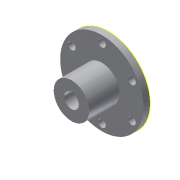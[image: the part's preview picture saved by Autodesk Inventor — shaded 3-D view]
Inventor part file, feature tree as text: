
AUTODESK INVENTOR PART (.ipt)
format: ipt  version: 2013 (Build 170138000, 138)  size: 117,760 bytes
history: native  units: in
note: dims shown in document units (in); Inventor stores cm internally (conversion verified against a paired STEP export)
features: extrude x4, sketch x4, pattern_circular x1
ambient origin geometry x8: Origin, YZ Plane, XZ Plane, XY Plane, X Axis, Y Axis, Z Axis, Center Point
bodies: Solid1 (feature_tree)
feature tree (9):
  extrude  "Extrusion1"  Depth=0.18in TaperAngle=0.0deg
  extrude  "Extrusion2"  Depth=0.82in TaperAngle=0.0deg
  extrude  "Extrusion3"  Depth=0.0984in
  extrude  "Extrusion4"  Depth=0.82in TaperAngle=0.0deg
  pattern_circular  "Circular Pattern1"  [2 undecoded]
  sketch  "Sketch1"  dims[d0=2.25in d1=0.18in d2=0.0in]
  sketch  "Sketch2"  dims[d3=0.958in d4=0.82in d5=0.0in]
  sketch  "Sketch3"  dims[d6=0.3937in d7=0.0984in]
  sketch  "Sketch4"  dims[d8=0.0984in d9=0.82in d10=0.0in d11=0.206in d12=0.9375in d13=1.0in d14=0.0in d15=2.3622in d16=360.0deg]
note: 2 required parameter values undecoded (feature->parameter linkage not recoverable at this tier; creation-order binding heuristic only, values carry confidence <= 0.55)
